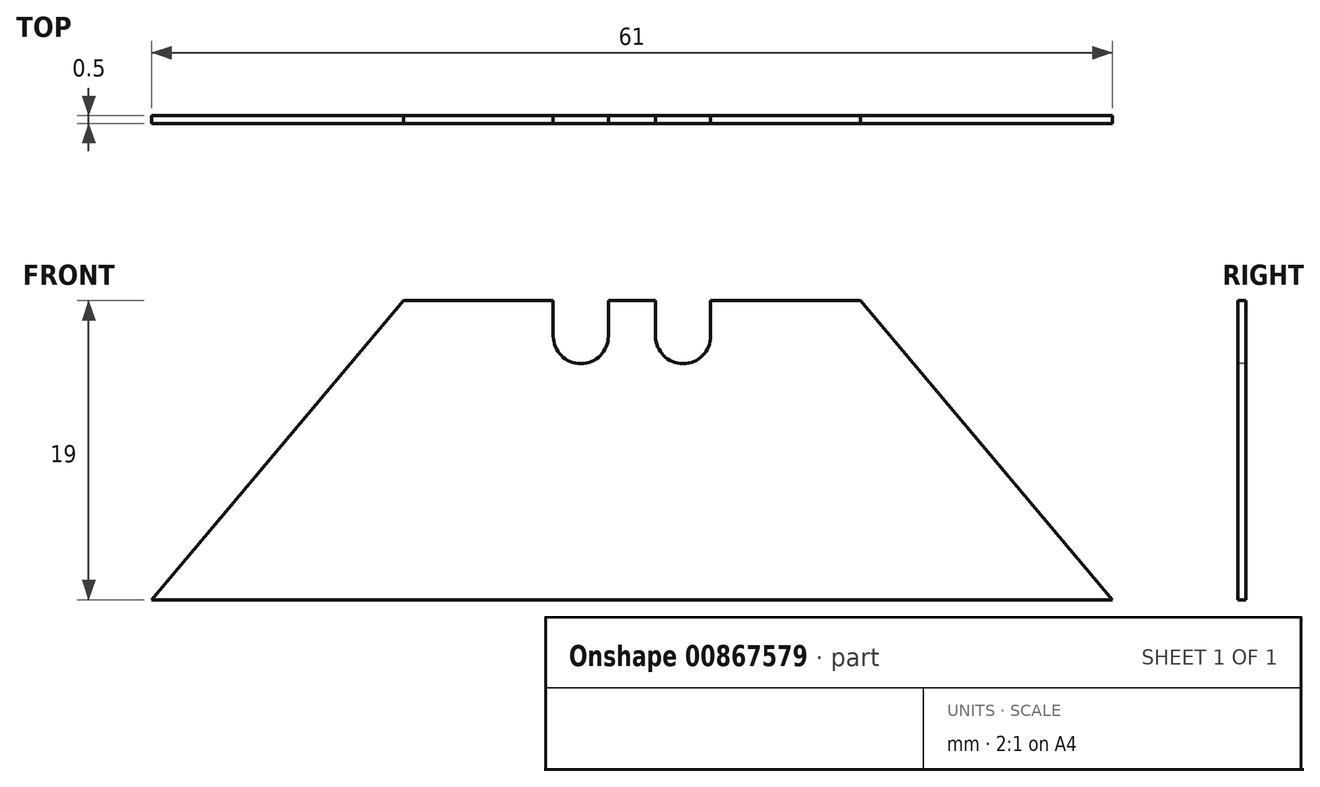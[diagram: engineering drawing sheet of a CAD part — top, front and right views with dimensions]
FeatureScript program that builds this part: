
annotation { "Feature Type Name" : "Feature", "Feature Type Description" : "" }
export const myFeature = defineFeature(function(context is Context, id is Id, definition is map)
    precondition{}
    {
        {
            var Q0;
            Q0=qCreatedBy(makeId("Front.planeOp"),FACE);
            var sketch = newSketch(context, id + "F0", { "sketchPlane" : qUnion([Q0])});
            skLineSegment(sketch, "E0", {"start": v(0, 0) * mm, "end": v(61, 0) * mm});
            skPoint(sketch, "E1", {"position": v(30.5, 0) * mm});
            skLineSegment(sketch, "E2", {"start": v(30.5, 0) * mm, "end": v(30.5, 19) * mm});
            skLineSegment(sketch, "E3", {"start": v(30.5, 19) * mm, "end": v(45, 19) * mm});
            skLineSegment(sketch, "E4", {"start": v(45, 19) * mm, "end": v(61, 0) * mm});
            skLineSegment(sketch, "E5", {"start": v(30.5, 19) * mm, "end": v(16, 19) * mm});
            skLineSegment(sketch, "E6", {"start": v(16, 19) * mm, "end": v(0, 0) * mm});
            skSolve(sketch);
        }
        {
            var Q0;
            {var subQ2=sQuery(id+"F0.wireOp",EDGE,"E2");Q0=makeQuery(id+"F0.imprint","IMPRINT",FACE,{"disambiguationData":[TD([[makeQuery(id+"F0.imprint","IMPRINT",EDGE,{"derivedFrom":subQ2}),1.0]])]});}
            var Q1;
            {var subQ2=sQuery(id+"F0.wireOp",EDGE,"E2");Q1=makeQuery(id+"F0.imprint","IMPRINT",FACE,{"disambiguationData":[TD([[makeQuery(id+"F0.imprint","IMPRINT",EDGE,{"derivedFrom":subQ2}),-1.0]])]});}
            extrude(context, id + "F1", {"entities" : qUnion([Q0, Q1]), "depth" : 0.5 * mm, "offsetDistance" : 25 * mm});
        }
        {
            var Q0;
            Q0=makeQuery(id+"F1.opExtrude","CAP_FACE",FACE,{"disambiguationData":[OSD([sQuery(id+"F0.wireOp",EDGE,"E0"),sQuery(id+"F0.wireOp",EDGE,"E3"),sQuery(id+"F0.wireOp",EDGE,"E4"),sQuery(id+"F0.wireOp",EDGE,"E5"),sQuery(id+"F0.wireOp",EDGE,"E6")])],"isStart":false});
            var sketch = newSketch(context, id + "F2", { "sketchPlane" : qUnion([Q0])});
            skPoint(sketch, "E7", {"position": v(30.5, 19) * mm});
            skLineSegment(sketch, "E8", {"start": v(30.5, 19) * mm, "end": v(32, 19) * mm});
            skLineSegment(sketch, "E9", {"start": v(30.5, 19) * mm, "end": v(29, 19) * mm});
            skPoint(sketch, "E10", {"position": v(33.75, 19) * mm});
            skPoint(sketch, "E11", {"position": v(27.25, 19) * mm});
            skPoint(sketch, "E12", {"position": v(33.75, 16.75) * mm});
            skPoint(sketch, "E13", {"position": v(27.25, 16.75) * mm});
            skCircle(sketch, "E14", {"center": v(33.75, 16.75) * mm, "radius": 1.75 * mm});
            skCircle(sketch, "E15", {"center": v(27.25, 16.75) * mm, "radius": 1.75 * mm});
            skLineSegment(sketch, "E16", {"start": v(29, 19) * mm, "end": v(29, 16.75) * mm});
            skLineSegment(sketch, "E17", {"start": v(32, 19) * mm, "end": v(32, 16.75) * mm});
            skPoint(sketch, "E18", {"position": v(25.5, 19) * mm});
            skPoint(sketch, "E19", {"position": v(35.5, 19) * mm});
            skLineSegment(sketch, "E20", {"start": v(35.5, 19) * mm, "end": v(35.5, 16.75) * mm});
            skLineSegment(sketch, "E21", {"start": v(25.5, 19) * mm, "end": v(25.5, 16.75) * mm});
            skSolve(sketch);
        }
        {
            var Q0;
            {var subQ0=sQuery(id+"F2.wireOp",EDGE,"E17");Q0=makeQuery(id+"F2.imprint","IMPRINT",FACE,{"disambiguationData":[TD([[makeQuery(id+"F2.imprint","IMPRINT",EDGE,{"derivedFrom":subQ0}),1.0]])]});}
            var Q1;
            {var subQ0=sQuery(id+"F2.wireOp",EDGE,"E14");var subQ1=makeQuery(id+"F2.imprint","INTERSECT",VERTEX,{"derivedFrom":[subQ0,sQuery(id+"F2.wireOp",EDGE,"E17")]});Q1=makeQuery(id+"F2.imprint","IMPRINT",FACE,{"disambiguationData":[TD([[makeQuery(id+"F2.imprint","IMPRINT",EDGE,{"disambiguationData":[TD([[subQ1,1.0]])],"derivedFrom":subQ0}),1.0]])]});}
            var Q2;
            {var subQ0=sQuery(id+"F2.wireOp",EDGE,"E15");var subQ1=makeQuery(id+"F2.imprint","INTERSECT",VERTEX,{"derivedFrom":[subQ0,sQuery(id+"F2.wireOp",EDGE,"E16")]});Q2=makeQuery(id+"F2.imprint","IMPRINT",FACE,{"disambiguationData":[TD([[makeQuery(id+"F2.imprint","IMPRINT",EDGE,{"disambiguationData":[TD([[subQ1,-1.0]])],"derivedFrom":subQ0}),1.0]])]});}
            var Q3;
            {var subQ0=sQuery(id+"F2.wireOp",EDGE,"E16");Q3=makeQuery(id+"F2.imprint","IMPRINT",FACE,{"disambiguationData":[TD([[makeQuery(id+"F2.imprint","IMPRINT",EDGE,{"derivedFrom":subQ0}),-1.0]])]});}
            extrude(context, id + "F3", {"entities" : qUnion([Q0, Q1, Q2, Q3]), "operationType" : NewBodyOperationType.REMOVE, "oppositeDirection" : true, "depth" : 25 * mm, "offsetDistance" : 25 * mm});
        }
    });
